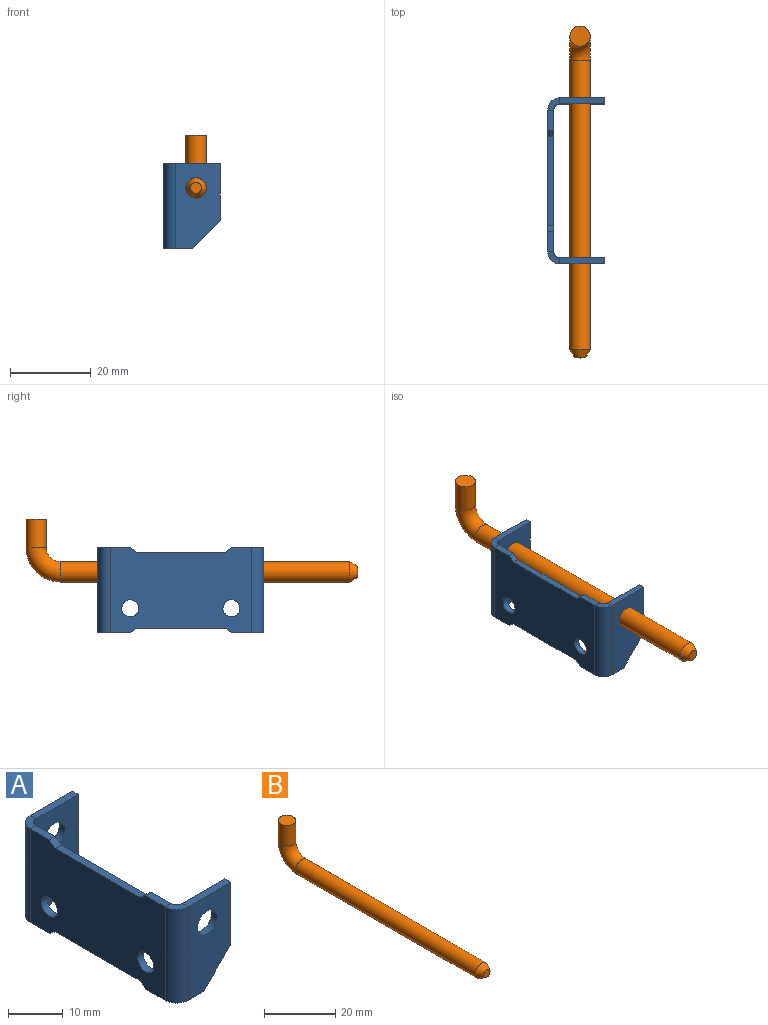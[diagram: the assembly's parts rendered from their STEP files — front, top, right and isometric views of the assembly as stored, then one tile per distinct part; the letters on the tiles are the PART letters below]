
ASSEMBLY  parts=2 mates=1
PART A: 36 faces, bbox 14x41x21 mm
  f0: plane 1.5x1.5mm, normal (0,0.6,0.8), area 2.8mm2, adj f1,f9,f12,f13
  f1: plane 22x1.5mm, normal (0,0,1), area 33mm2, adj f0,f2,f12,f13
  f2: plane 1.5x1.5mm, normal (0,-0.6,0.8), area 2.8mm2, adj f1,f3,f12,f13
  f3: plane 5x1.5mm, normal (0,0,1), area 7.5mm2, adj f2,f12,f13,f32
  f4: plane 5x1.5mm, normal (0,0,-1), area 7.5mm2, adj f5,f12,f13,f33
  f5: plane 1.5x1.5mm, normal (0,-0.6,-0.8), area 2.8mm2, adj f4,f6,f12,f13
  f6: plane 22x1.5mm, normal (0,0,-1), area 33mm2, adj f5,f7,f12,f13
  f7: plane 1.5x1.5mm, normal (0,0.6,-0.8), area 2.8mm2, adj f6,f8,f12,f13
  f8: plane 5x1.5mm, normal (0,0,-1), area 7.5mm2, adj f7,f12,f13,f21
  f9: plane 5x1.5mm, normal (0,0,1), area 7.5mm2, adj f0,f12,f13,f22
  f10: cylinder r=2.1mm len=4.2mm, axis (1,0,0), area 19.8mm2, adj f12,f13
  f11: cylinder r=2.1mm len=4.2mm, axis (1,0,0), area 19.8mm2, adj f12,f13
  f12: plane 35x21mm, normal (-1,0,0), area 653.8mm2, adj f0,f1,f2,f3,f4,f5,f6,f7
  f13: plane 35x21mm, normal (1,0,0), area 653.8mm2, adj f0,f1,f2,f3,f4,f5,f6,f7
  f14: plane 14x1.5mm, normal (1,0,0), area 21mm2, adj f15,f18,f19,f20
  f15: plane 11x1.5mm, normal (0,0,1), area 16.5mm2, adj f14,f18,f19,f22
  f16: cylinder r=2.55mm len=5.1mm, axis (0,-1,0), area 24mm2, adj f18,f19
  f17: plane 4x1.5mm, normal (0,0,-1), area 6mm2, adj f18,f19,f20,f21
  f18: plane 21x11mm, normal (0,-1,0), area 186.1mm2, adj f14,f15,f16,f17,f20,f23
  f19: plane 21x11mm, normal (0,1,0), area 186.1mm2, adj f14,f15,f16,f17,f20,f24
  f20: plane 7x7mm, normal (0.71,0,-0.71), area 14.8mm2, adj f14,f17,f18,f19
  f21: plane 3x3mm, normal (0,0,-1), area 5.3mm2, adj f8,f17,f23,f24
  f22: plane 3x3mm, normal (0,0,1), area 5.3mm2, adj f9,f15,f23,f24
  f23: cylinder r=3mm len=21mm, axis (0,0,-1), area 99mm2, adj f12,f18,f21,f22
  f24: cylinder r=1.5mm len=21mm, axis (0,0,-1), area 49.5mm2, adj f13,f19,f21,f22
  f25: plane 14x1.5mm, normal (1,0,0), area 21mm2, adj f28,f29,f30,f31
  f26: plane 4x1.5mm, normal (0,0,-1), area 6mm2, adj f29,f30,f31,f33
  f27: cylinder r=2.55mm len=5.1mm, axis (0,1,0), area 24mm2, adj f29,f30
  f28: plane 11x1.5mm, normal (0,0,1), area 16.5mm2, adj f25,f29,f30,f32
  f29: plane 21x11mm, normal (0,1,0), area 186.1mm2, adj f25,f26,f27,f28,f31,f34
  f30: plane 21x11mm, normal (0,-1,0), area 186.1mm2, adj f25,f26,f27,f28,f31,f35
  f31: plane 7x7mm, normal (0.71,0,-0.71), area 14.8mm2, adj f25,f26,f29,f30
  f32: plane 3x3mm, normal (0,0,1), area 5.3mm2, adj f3,f28,f34,f35
  f33: plane 3x3mm, normal (0,0,-1), area 5.3mm2, adj f4,f26,f34,f35
  f34: cylinder r=3mm len=21mm, axis (0,0,1), area 99mm2, adj f12,f29,f32,f33
  f35: cylinder r=1.5mm len=21mm, axis (0,0,1), area 49.5mm2, adj f13,f30,f32,f33
PART B: 6 faces, bbox 5x82.7x16.2 mm
  f0: plane 2.69x2.69mm, normal (0,-1,0), area 5.7mm2, adj f5
  f1: plane 5x5mm, normal (0,0,1), area 19.6mm2, adj f4
  f2: cylinder r=2.5mm len=71.5mm, axis (0,1,0), area 1123.1mm2, adj f3,f5
  f3: torus R=6mm, axis (1,0,0), area 148mm2, adj f2,f4
  f4: cylinder r=2.5mm len=6.98mm, axis (0,0,1), area 109.7mm2, adj f1,f3
  f5: cone r=2.5mm half-angle=30deg, axis (0,1,0), area 27.9mm2, adj f0,f2
PLACE A rot(axis=(0.37,0.14,-0.92),0deg) t=(-3.62,-16.28,-0.65)mm
PLACE B rot(axis=(0.37,0.14,-0.92),0deg) t=(-3.62,-16.53,-0.65)mm
MATE slider B.f2 <-> A.f16  axis (0,1,0) through (4.38,-22.28,14.35)mm
